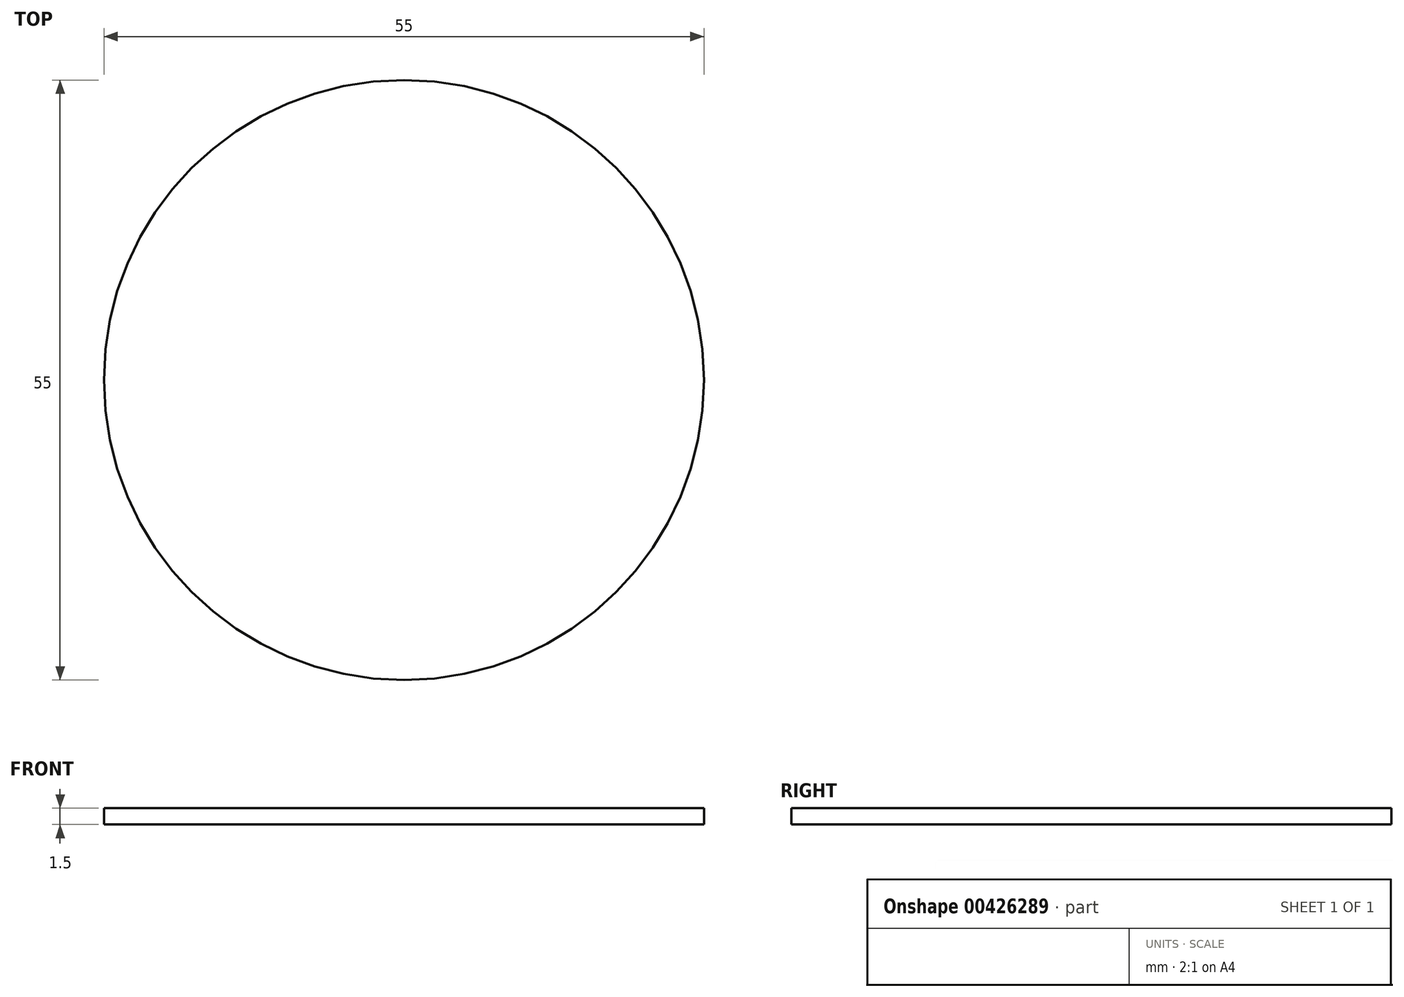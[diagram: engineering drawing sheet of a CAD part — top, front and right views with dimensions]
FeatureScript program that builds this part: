
annotation { "Feature Type Name" : "Feature", "Feature Type Description" : "" }
export const myFeature = defineFeature(function(context is Context, id is Id, definition is map)
    precondition{}
    {
        {
            var Q0;
            Q0=qCreatedBy(makeId("Top.planeOp"),FACE);
            var sketch = newSketch(context, id + "F0", { "sketchPlane" : qUnion([Q0])});
            skCircle(sketch, "E0", {"center": v(0, 0) * mm, "radius": 27.5 * mm});
            skSolve(sketch);
        }
        {
            var Q0;
            Q0=makeQuery(id+"F0.imprint","IMPRINT",FACE,{"disambiguationData":[TD([[makeQuery(id+"F0.imprint","IMPRINT",EDGE,{"derivedFrom":sQuery(id+"F0.wireOp",EDGE,"E0")}),1.0]])]});
            var Q1;
            Q1=sQuery(id+"F0.wireOp",EDGE,"E0");
            extrude(context, id + "F1", {"entities" : qUnion([Q0]), "surfaceEntities" : qUnion([Q1]), "depth" : 1.5 * mm});
        }
    });
